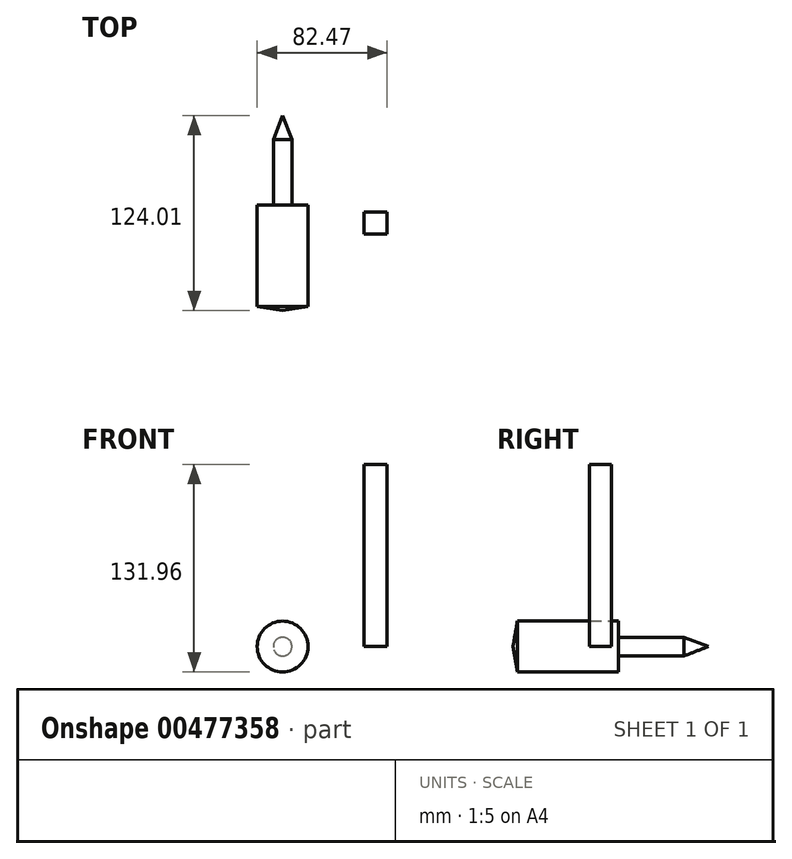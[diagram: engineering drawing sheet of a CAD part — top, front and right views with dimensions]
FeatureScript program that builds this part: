
annotation { "Feature Type Name" : "Feature", "Feature Type Description" : "" }
export const myFeature = defineFeature(function(context is Context, id is Id, definition is map)
    precondition{}
    {
        {
            var Q0;
            Q0=qCreatedBy(makeId("Top.planeOp"),FACE);
            var sketch = newSketch(context, id + "F0", { "sketchPlane" : qUnion([Q0])});
            skLineSegment(sketch, "E0", {"start": v(-59.57, -64.23) * mm, "end": v(-59.57, 0) * mm});
            skLineSegment(sketch, "E1", {"start": v(-59.57, 0) * mm, "end": v(-49.35, 0) * mm});
            skLineSegment(sketch, "E2", {"start": v(-49.35, 0) * mm, "end": v(-49.35, 41.6) * mm});
            skLineSegment(sketch, "E3", {"start": v(-49.35, 41.6) * mm, "end": v(-43.42, 57) * mm});
            skLineSegment(sketch, "E4", {"start": v(-43.42, 57) * mm, "end": v(-43.42, -67) * mm});
            skLineSegment(sketch, "E5", {"start": v(-43.42, -67) * mm, "end": v(-59.57, -64.23) * mm});
            skSolve(sketch);
        }
        {
            var Q0;
            Q0 = qSketchRegion(id + "F0", true);
            var Q1;
            Q1=sQuery(id+"F0.wireOp",EDGE,"E4");
            revolve(context, id + "F1", {"entities" : qUnion([Q0]), "axis" : qUnion([Q1]), "revolveType" : RevolveType.FULL});
        }
        {
            var Q0;
            Q0=qCreatedBy(makeId("Top.planeOp"),FACE);
            var sketch = newSketch(context, id + "F2", { "sketchPlane" : qUnion([Q0])});
            skLineSegment(sketch, "E6.bottom", {"start": v(8.2, -18.32) * mm, "end": v(22.9, -18.32) * mm});
            skLineSegment(sketch, "E6.top", {"start": v(8.2, -4.42) * mm, "end": v(22.9, -4.42) * mm});
            skLineSegment(sketch, "E6.left", {"start": v(8.2, -18.32) * mm, "end": v(8.2, -4.42) * mm});
            skLineSegment(sketch, "E6.right", {"start": v(22.9, -18.32) * mm, "end": v(22.9, -4.42) * mm});
            skSolve(sketch);
        }
        {
            var Q0;
            Q0 = qSketchRegion(id + "F2", true);
            extrude(context, id + "F3", {"entities" : qUnion([Q0]), "depth" : 115.82 * mm});
        }
    });
